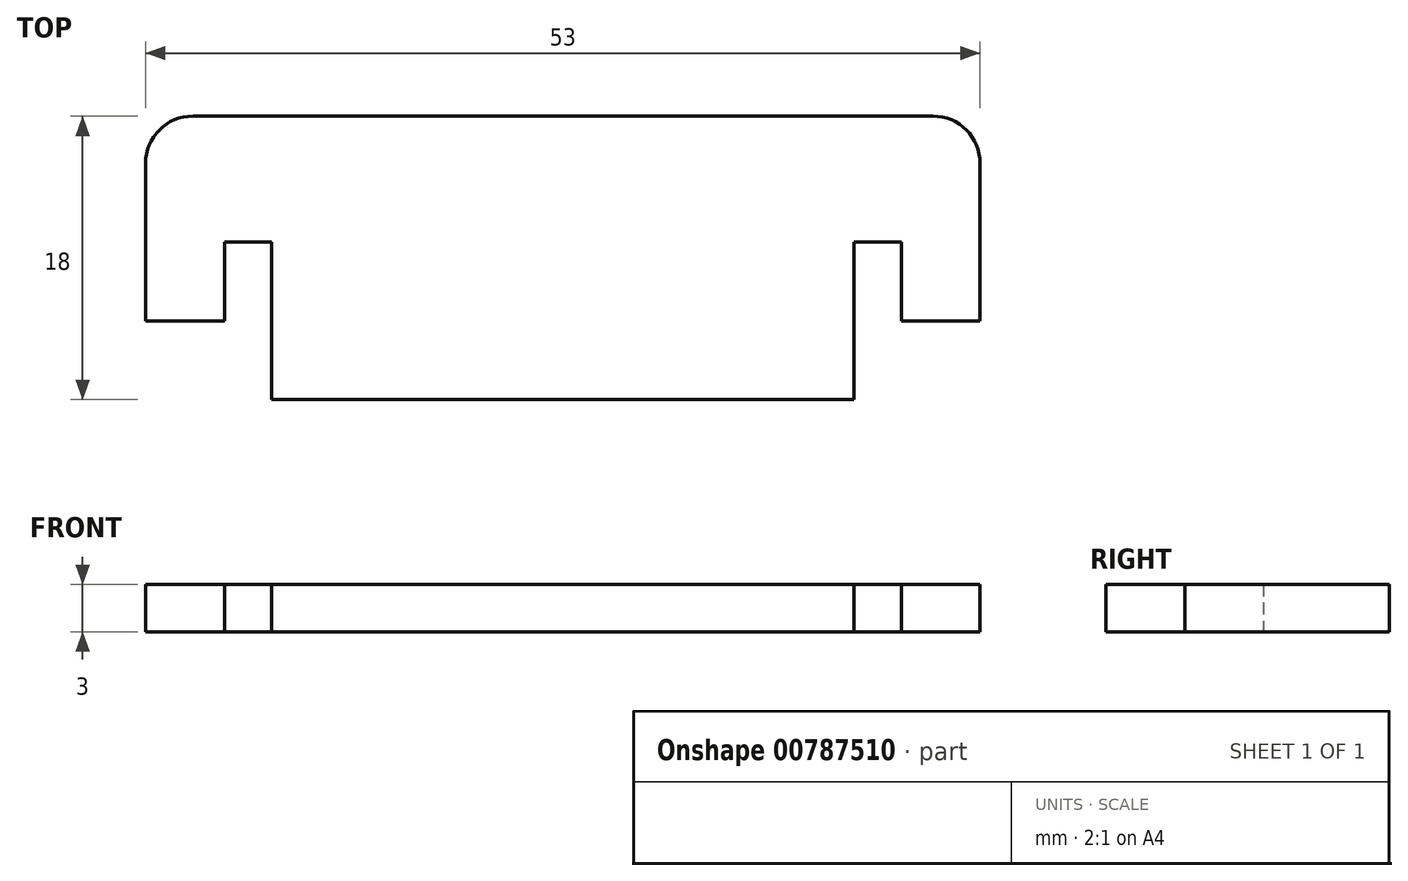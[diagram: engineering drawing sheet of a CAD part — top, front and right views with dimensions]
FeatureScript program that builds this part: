
annotation { "Feature Type Name" : "Feature", "Feature Type Description" : "" }
export const myFeature = defineFeature(function(context is Context, id is Id, definition is map)
    precondition{}
    {
        {
            var Q0;
            Q0=qCreatedBy(makeId("Top.planeOp"),FACE);
            var sketch = newSketch(context, id + "F0", { "sketchPlane" : qUnion([Q0])});
            skLineSegment(sketch, "E0", {"start": v(-25.3, 19.52) * mm, "end": v(21.7, 19.52) * mm});
            skLineSegment(sketch, "E1", {"start": v(24.7, 16.52) * mm, "end": v(24.7, 6.52) * mm});
            skLineSegment(sketch, "E2", {"start": v(24.7, 6.52) * mm, "end": v(19.7, 6.52) * mm});
            skLineSegment(sketch, "E3", {"start": v(19.7, 6.52) * mm, "end": v(19.7, 11.52) * mm});
            skLineSegment(sketch, "E4", {"start": v(19.7, 11.52) * mm, "end": v(16.7, 11.52) * mm});
            skLineSegment(sketch, "E5", {"start": v(16.7, 11.52) * mm, "end": v(16.7, 1.52) * mm});
            skLineSegment(sketch, "E6", {"start": v(16.7, 1.52) * mm, "end": v(-20.3, 1.52) * mm});
            skLineSegment(sketch, "E7", {"start": v(-20.3, 1.52) * mm, "end": v(-20.3, 11.52) * mm});
            skLineSegment(sketch, "E8", {"start": v(-20.3, 11.52) * mm, "end": v(-23.3, 11.52) * mm});
            skLineSegment(sketch, "E9", {"start": v(-23.3, 11.52) * mm, "end": v(-23.3, 6.52) * mm});
            skLineSegment(sketch, "E10", {"start": v(-23.3, 6.52) * mm, "end": v(-28.3, 6.52) * mm});
            skLineSegment(sketch, "E11", {"start": v(-28.3, 6.52) * mm, "end": v(-28.3, 16.52) * mm});
            skPoint(sketch, "E12", {"position": v(-21.8, 11.52) * mm});
            skPoint(sketch, "E13", {"position": v(18.2, 11.52) * mm});
            skPoint(sketch, "E14.visualSharp", {"position": v(-28.3, 19.52) * mm});
            skArc(sketch, "E14.filletArc", {"start": v(-25.3, 19.52) * mm, "mid": v(-27.41, 18.64) * mm, "end": v(-28.3, 16.52) * mm});
            skPoint(sketch, "E15.visualSharp", {"position": v(24.7, 19.52) * mm});
            skArc(sketch, "E15.filletArc", {"start": v(24.7, 16.52) * mm, "mid": v(23.83, 18.64) * mm, "end": v(21.7, 19.52) * mm});
            skSolve(sketch);
        }
        {
            var Q0;
            Q0=makeQuery(id+"F0.imprint","IMPRINT",FACE,{"disambiguationData":[TD([[makeQuery(id+"F0.imprint","IMPRINT",EDGE,{"derivedFrom":sQuery(id+"F0.wireOp",EDGE,"E0")}),-1.0]])]});
            extrude(context, id + "F1", {"entities" : qUnion([Q0]), "depth" : 3 * mm, "offsetDistance" : 25.4 * mm});
        }
    });
